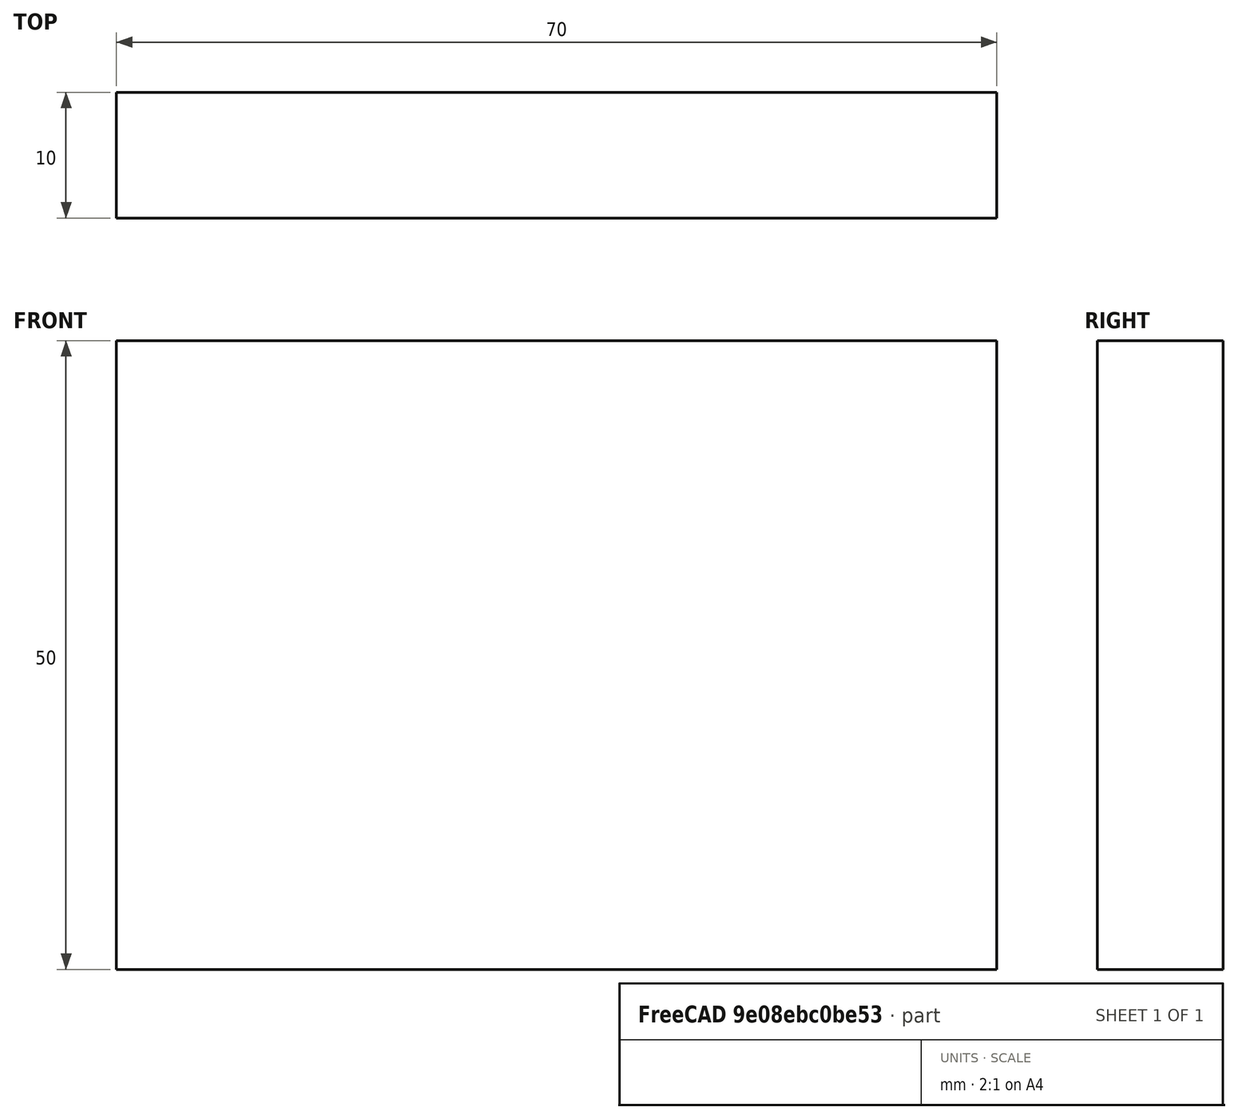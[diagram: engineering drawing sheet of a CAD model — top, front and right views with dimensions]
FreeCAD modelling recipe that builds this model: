
FCSTD DOCUMENT  (FreeCAD 0.15R4671 (Git))
Label: Flat Bar 70x10 EN10058 S235JR
License: All rights reserved
LicenseURL: http://en.wikipedia.org/wiki/All_rights_reserved
objects: Sketcher::SketchObject×1, Part::Extrusion×1
note: 2 computed .brp shape members not serialized (recipe doc carries the construction recipe); baked Part::Feature solids carry a one-line shape summary decoded from their .brp

FEATURE [Sketcher::SketchObject] Sketch
  sketch-geometry (4):
    g0: LineSegment StartX=-35 StartY=-5 StartZ=0 EndX=35 EndY=-5 EndZ=0
    g1: LineSegment StartX=35 StartY=-5 StartZ=0 EndX=35 EndY=5 EndZ=0
    g2: LineSegment StartX=35 StartY=5 StartZ=0 EndX=-35 EndY=5 EndZ=0
    g3: LineSegment StartX=-35 StartY=5 StartZ=0 EndX=-35 EndY=-5 EndZ=0
  constraints (12):
    c: Coincident(g0,g1)
    c: Coincident(g1,g2)
    c: Coincident(g2,g3)
    c: Coincident(g3,g0)
    c: Horizontal(g0)
    c: Horizontal(g2)
    c: Vertical(g1)
    c: Vertical(g3)
    c: Symmetric(g1,g2,g-2)
    c: Symmetric(g0,g1,g-1)
    c: DistanceY(g1) = 10
    c: DistanceX(g0) = 70
FEATURE [Part::Extrusion] Extrude  label="Flat Bar 70x10 EN10058 S235JR"
  Base = -> Sketch
  Dir = (0,0,50)
  Solid = true
